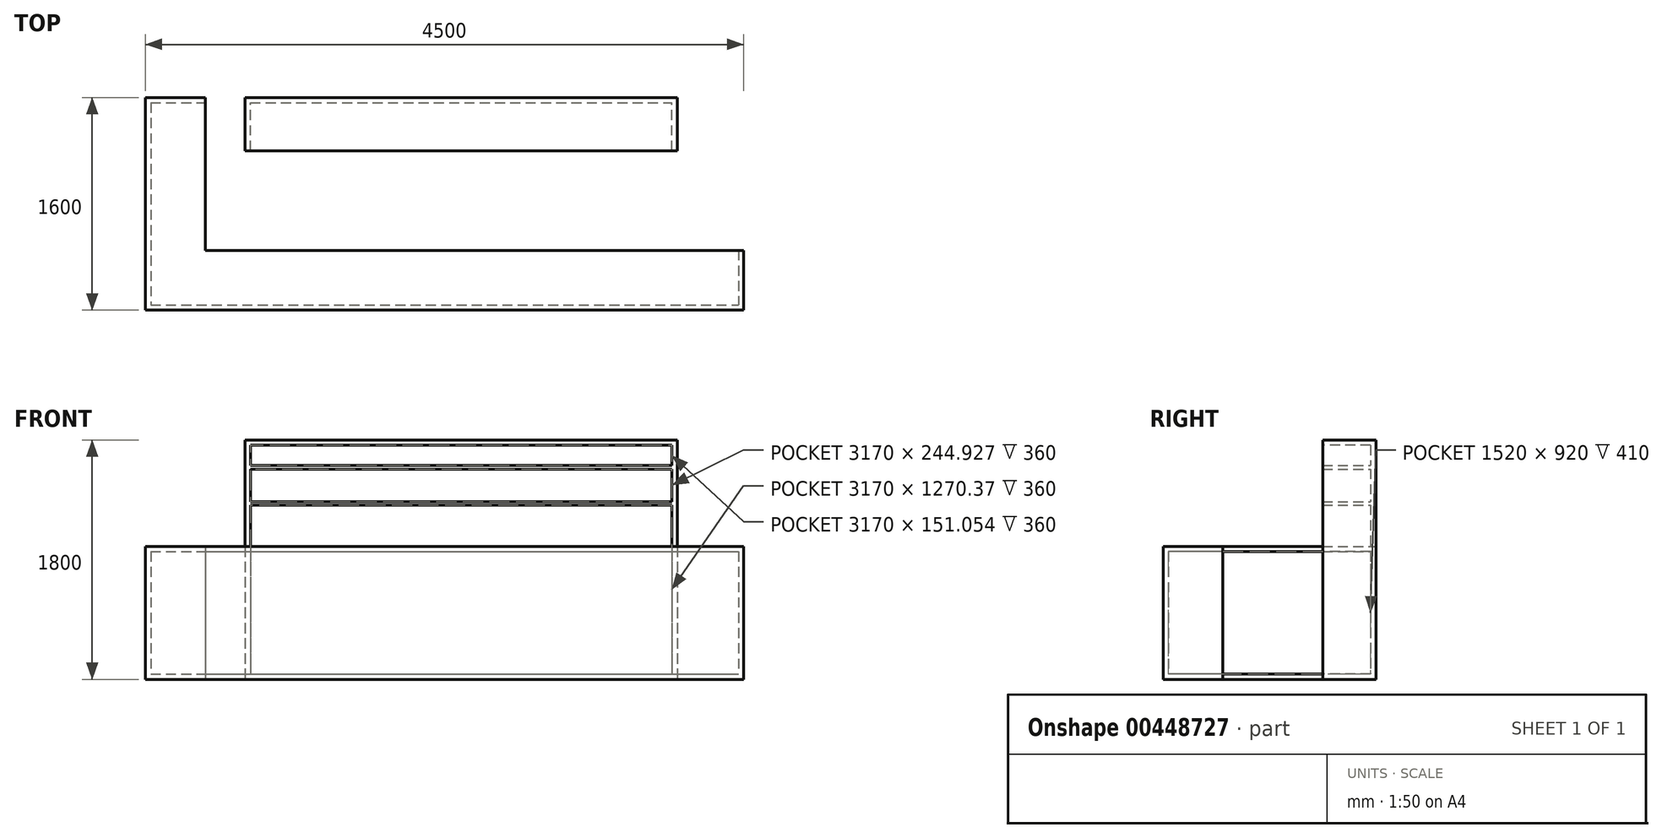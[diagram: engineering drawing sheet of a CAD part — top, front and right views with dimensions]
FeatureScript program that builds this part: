
annotation { "Feature Type Name" : "Feature", "Feature Type Description" : "" }
export const myFeature = defineFeature(function(context is Context, id is Id, definition is map)
    precondition{}
    {
        {
            var Q0;
            Q0=qCreatedBy(makeId("Top.planeOp"),FACE);
            var sketch = newSketch(context, id + "F0", { "sketchPlane" : qUnion([Q0])});
            skLineSegment(sketch, "E0.bottom", {"start": v(-1083.6, 404.26) * mm, "end": v(2966.4, 404.26) * mm});
            skLineSegment(sketch, "E0.top", {"start": v(-1533.6, -45.74) * mm, "end": v(2966.4, -45.74) * mm});
            skLineSegment(sketch, "E0.left", {"start": v(-1533.6, 404.26) * mm, "end": v(-1533.6, -45.74) * mm});
            skLineSegment(sketch, "E0.right", {"start": v(2966.4, 404.26) * mm, "end": v(2966.4, -45.74) * mm});
            skLineSegment(sketch, "E1.top", {"start": v(-1533.6, 1554.26) * mm, "end": v(-1083.6, 1554.26) * mm});
            skLineSegment(sketch, "E1.left", {"start": v(-1533.6, 404.26) * mm, "end": v(-1533.6, 1554.26) * mm});
            skLineSegment(sketch, "E1.right", {"start": v(-1083.6, 404.26) * mm, "end": v(-1083.6, 1554.26) * mm});
            skLineSegment(sketch, "E2.bottom", {"start": v(-783.6, 1554.26) * mm, "end": v(2466.4, 1554.26) * mm});
            skLineSegment(sketch, "E2.top", {"start": v(-783.6, 1154.26) * mm, "end": v(2466.4, 1154.26) * mm});
            skLineSegment(sketch, "E2.left", {"start": v(-783.6, 1554.26) * mm, "end": v(-783.6, 1154.26) * mm});
            skLineSegment(sketch, "E2.right", {"start": v(2466.4, 1554.26) * mm, "end": v(2466.4, 1154.26) * mm});
            skSolve(sketch);
        }
        {
            var Q0;
            Q0=makeQuery(id+"F0.imprint","IMPRINT",FACE,{"disambiguationData":[TD([[makeQuery(id+"F0.imprint","IMPRINT",EDGE,{"derivedFrom":sQuery(id+"F0.wireOp",EDGE,"E0.bottom")}),-1.0]])]});
            extrude(context, id + "F1", {"entities" : qUnion([Q0]), "depth" : 1000 * mm});
        }
        {
            var Q0;
            Q0=makeQuery(id+"F0.imprint","IMPRINT",FACE,{"disambiguationData":[TD([[makeQuery(id+"F0.imprint","IMPRINT",EDGE,{"derivedFrom":sQuery(id+"F0.wireOp",EDGE,"E2.bottom")}),-1.0]])]});
            extrude(context, id + "F2", {"entities" : qUnion([Q0]), "depth" : 1800 * mm});
        }
        {
            var Q0;
            Q0=makeQuery(id+"F2.opExtrude","SWEPT_FACE",FACE,{"disambiguationData":[OSD([sQuery(id+"F0.wireOp",EDGE,"E2.top")])]});
            shell(context, id + "F3", {"entities" : qUnion([Q0]), "thickness" : 40 * mm});
        }
        {
            var Q0;
            Q0=makeQuery(id+"F1.opExtrude","SWEPT_FACE",FACE,{"disambiguationData":[OSD([sQuery(id+"F0.wireOp",EDGE,"E0.bottom")])]});
            var Q1;
            Q1=makeQuery(id+"F1.opExtrude","SWEPT_FACE",FACE,{"disambiguationData":[OSD([sQuery(id+"F0.wireOp",EDGE,"E1.right")])]});
            shell(context, id + "F4", {"entities" : qUnion([Q0, Q1]), "thickness" : 40 * mm});
        }
        {
            var Q0;
            Q0=makeQuery(id+"F3.opShell","OFFSET_FACE",FACE,{"disambiguationData":[OSD([sQuery(id+"F0.wireOp",EDGE,"E2.bottom")])]});
            var sketch = newSketch(context, id + "F5", { "sketchPlane" : qUnion([Q0])});
            skLineSegment(sketch, "E3.bottom", {"start": v(-743.6, 1336.03) * mm, "end": v(2426.4, 1336.03) * mm});
            skLineSegment(sketch, "E3.top", {"start": v(-743.6, 1310.37) * mm, "end": v(2426.4, 1310.37) * mm});
            skLineSegment(sketch, "E3.left", {"start": v(-743.6, 1336.03) * mm, "end": v(-743.6, 1310.37) * mm});
            skLineSegment(sketch, "E3.right", {"start": v(2426.4, 1336.03) * mm, "end": v(2426.4, 1310.37) * mm});
            skLineSegment(sketch, "E4.bottom", {"start": v(-743.6, 1608.95) * mm, "end": v(2426.4, 1608.95) * mm});
            skLineSegment(sketch, "E4.top", {"start": v(-743.6, 1580.95) * mm, "end": v(2426.4, 1580.95) * mm});
            skLineSegment(sketch, "E4.left", {"start": v(-743.6, 1608.95) * mm, "end": v(-743.6, 1580.95) * mm});
            skLineSegment(sketch, "E4.right", {"start": v(2426.4, 1608.95) * mm, "end": v(2426.4, 1580.95) * mm});
            skSolve(sketch);
        }
        {
            var Q0;
            Q0 = qSketchRegion(id + "F5", true);
            extrude(context, id + "F6", {"entities" : qUnion([Q0]), "operationType" : NewBodyOperationType.ADD, "depth" : 360 * mm});
        }
    });
